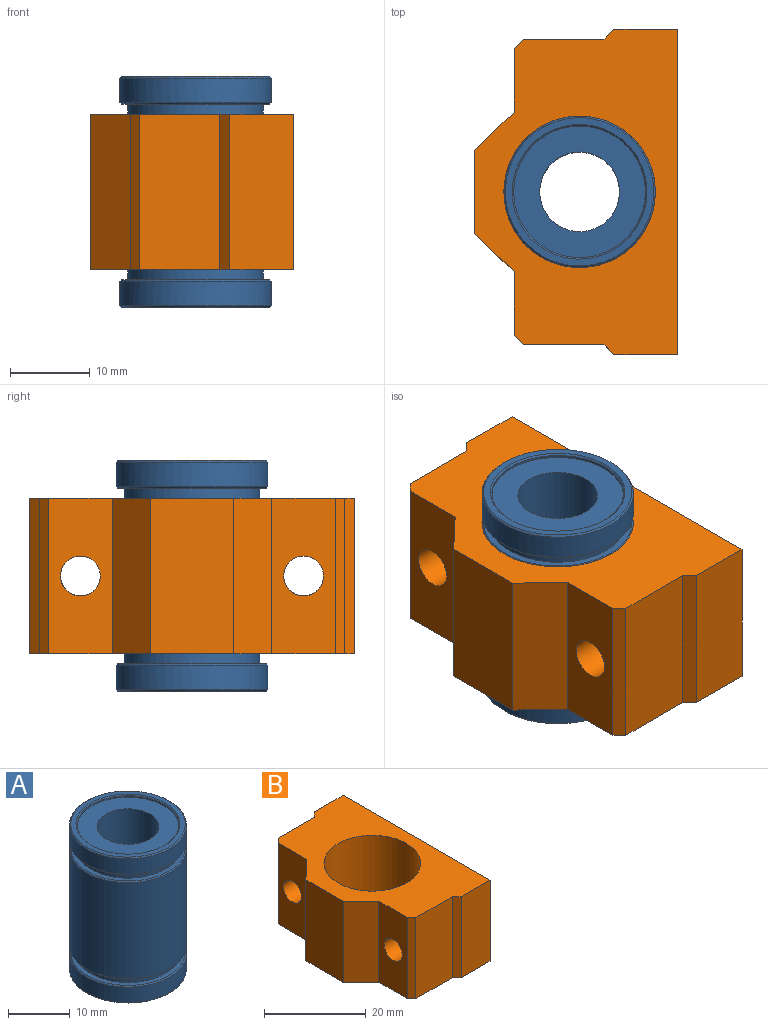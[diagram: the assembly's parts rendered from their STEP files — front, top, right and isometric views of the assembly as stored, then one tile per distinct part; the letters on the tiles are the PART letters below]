
ASSEMBLY  parts=2 mates=1
PART A: 24 faces, bbox 19x19x29 mm
  f0: cylinder r=9.5mm len=19mm, axis (0,0,-1), area 185mm2, adj f17,f19
  f1: cylinder r=8.25mm len=16.5mm, axis (0,0,-1), area 15.6mm2, adj f8,f16
  f2: cylinder r=8.25mm len=16.5mm, axis (0,0,-1), area 15.6mm2, adj f7,f22
  f3: cylinder r=9.5mm len=19mm, axis (0,0,-1), area 185mm2, adj f20,f23
  f4: plane 18.6x18.6mm, normal (0,0,1), area 47.4mm2, adj f22,f23
  f5: plane 18.6x18.6mm, normal (0,0,-1), area 47.4mm2, adj f16,f17
  f6: cylinder r=5mm len=28mm, axis (0,0,-1), area 879.6mm2, adj f7,f8
  f7: plane 16.5x16.5mm, normal (0,0,1), area 135.3mm2, adj f2,f6
  f8: plane 16.5x16.5mm, normal (0,0,-1), area 135.3mm2, adj f1,f6
  f9: plane 18.6x18.6mm, normal (0,0,-1), area 44.7mm2, adj f11,f18
  f10: plane 18.6x18.6mm, normal (0,0,1), area 44.7mm2, adj f11,f19
  f11: cylinder r=8.5mm len=17mm, axis (0,0,1), area 66.8mm2, adj f9,f10
  f12: cylinder r=9.5mm len=19.1mm, axis (0,0,-1), area 1140.1mm2, adj f18,f21
  f13: plane 18.6x18.6mm, normal (0,0,1), area 44.7mm2, adj f14,f21
  f14: cylinder r=8.5mm len=17mm, axis (0,0,1), area 66.8mm2, adj f13,f15
  f15: plane 18.6x18.6mm, normal (0,0,-1), area 44.7mm2, adj f14,f20
  f16: cone r=8.45mm half-angle=45deg, axis (0,0,-1), area 14.8mm2, adj f1,f5
  f17: cone r=9.5mm half-angle=45deg, axis (0,0,1), area 16.7mm2, adj f0,f5
  f18: cone r=9.5mm half-angle=45deg, axis (0,0,1), area 16.7mm2, adj f9,f12
  f19: cone r=9.3mm half-angle=45deg, axis (0,0,-1), area 16.7mm2, adj f0,f10
  f20: cone r=9.5mm half-angle=45deg, axis (0,0,1), area 16.7mm2, adj f3,f15
  f21: cone r=9.3mm half-angle=45deg, axis (0,0,-1), area 16.7mm2, adj f12,f13
  f22: cone r=8.25mm half-angle=45deg, axis (0,0,1), area 14.8mm2, adj f2,f4
  f23: cone r=9.3mm half-angle=45deg, axis (0,0,-1), area 16.7mm2, adj f3,f4
PART B: 19 faces, bbox 25.5x40.8x19.5 mm
  f0: plane 19.5x8mm, normal (0,1,0), area 156mm2, adj f1,f14,f15,f16
  f1: plane 19.5x1.25mm, normal (-0.71,0.71,0), area 34.5mm2, adj f0,f2,f15,f16
  f2: plane 19.5x10.1mm, normal (0,1,0), area 196.9mm2, adj f1,f3,f15,f16
  f3: plane 19.5x1.15mm, normal (-0.71,0.71,0), area 31.7mm2, adj f2,f4,f15,f16
  f4: plane 19.5x8mm, normal (-1,0,0), area 136.4mm2, adj f3,f5,f15,f16,f17
  f5: plane 19.5x5mm, normal (-0.69,0.72,0), area 134.5mm2, adj f4,f6,f15,f16
  f6: plane 19.5x10.5mm, normal (-1,0,0), area 204.8mm2, adj f5,f7,f15,f16
  f7: plane 19.5x5mm, normal (-0.69,-0.72,0), area 134.5mm2, adj f6,f8,f15,f16
  f8: plane 19.5x8mm, normal (-1,0,0), area 136.4mm2, adj f7,f9,f15,f16,f18
  f9: plane 19.5x1.15mm, normal (-0.71,-0.71,0), area 31.7mm2, adj f8,f10,f15,f16
  f10: plane 19.5x10.1mm, normal (0,-1,0), area 197mm2, adj f9,f11,f15,f16
  f11: plane 19.5x1.25mm, normal (-0.71,-0.71,0), area 34.5mm2, adj f10,f12,f15,f16
  f12: plane 19.5x8mm, normal (0,-1,0), area 156mm2, adj f11,f14,f15,f16
  f13: cylinder r=9.5mm len=19.5mm, axis (0,0,-1), area 1164mm2, adj f15,f16
  f14: plane 40.8x19.5mm, normal (1,0,0), area 756.3mm2, adj f0,f12,f15,f16,f17,f18
  f15: plane 40.8x25.5mm, normal (0,0,1), area 598.1mm2, adj f0,f1,f2,f3,f4,f5,f6,f7
  f16: plane 40.8x25.5mm, normal (0,0,-1), area 598.1mm2, adj f0,f1,f2,f3,f4,f5,f6,f7
  f17: cylinder r=2.5mm len=20.5mm, axis (-1,0,0), area 322mm2, adj f4,f14
  f18: cylinder r=2.5mm len=20.5mm, axis (-1,0,0), area 322mm2, adj f8,f14
PLACE A t=(0,0,-4.75)mm
PLACE B at identity
MATE fastened A.f0 <-> B.f13  axis (0,0,1) through (0,0,24.25)mm
